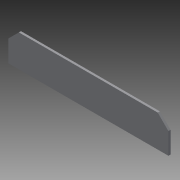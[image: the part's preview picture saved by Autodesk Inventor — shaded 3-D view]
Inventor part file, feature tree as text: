
AUTODESK INVENTOR PART (.ipt)
format: ipt  version: 2014 (Build 180170000, 170)  size: 844,800 bytes
history: native  units: mm
features: extrude x3, sketch x3, chamfer x1
ambient origin geometry x8: Origin, YZ Plane, XZ Plane, XY Plane, X Axis, Y Axis, Z Axis, Center Point
bodies: Solid1 (feature_tree)
feature tree (7):
  extrude  "Extrusion1"  Depth=30.0mm
  chamfer  "Chamfer1"  Distance=2.0mm
  extrude  "Extrusion2"  Depth=10.0mm TaperAngle=0.0deg
  extrude  "Extrusion3"  Depth=3.0mm
  sketch  "Sketch1"  dims[d0=150.0mm d1=30.0mm d2=2.0mm d3=0.0mm]
  sketch  "Sketch2"  dims[d4=10.0mm d5=2.0mm d6=45.0deg d7=1.2mm d8=0.0mm]
  sketch  "Sketch3"  dims[d9=3.0mm d10=3.0mm d11=15.0mm d12=15.0mm d13=1.2mm d14=0.0mm]
